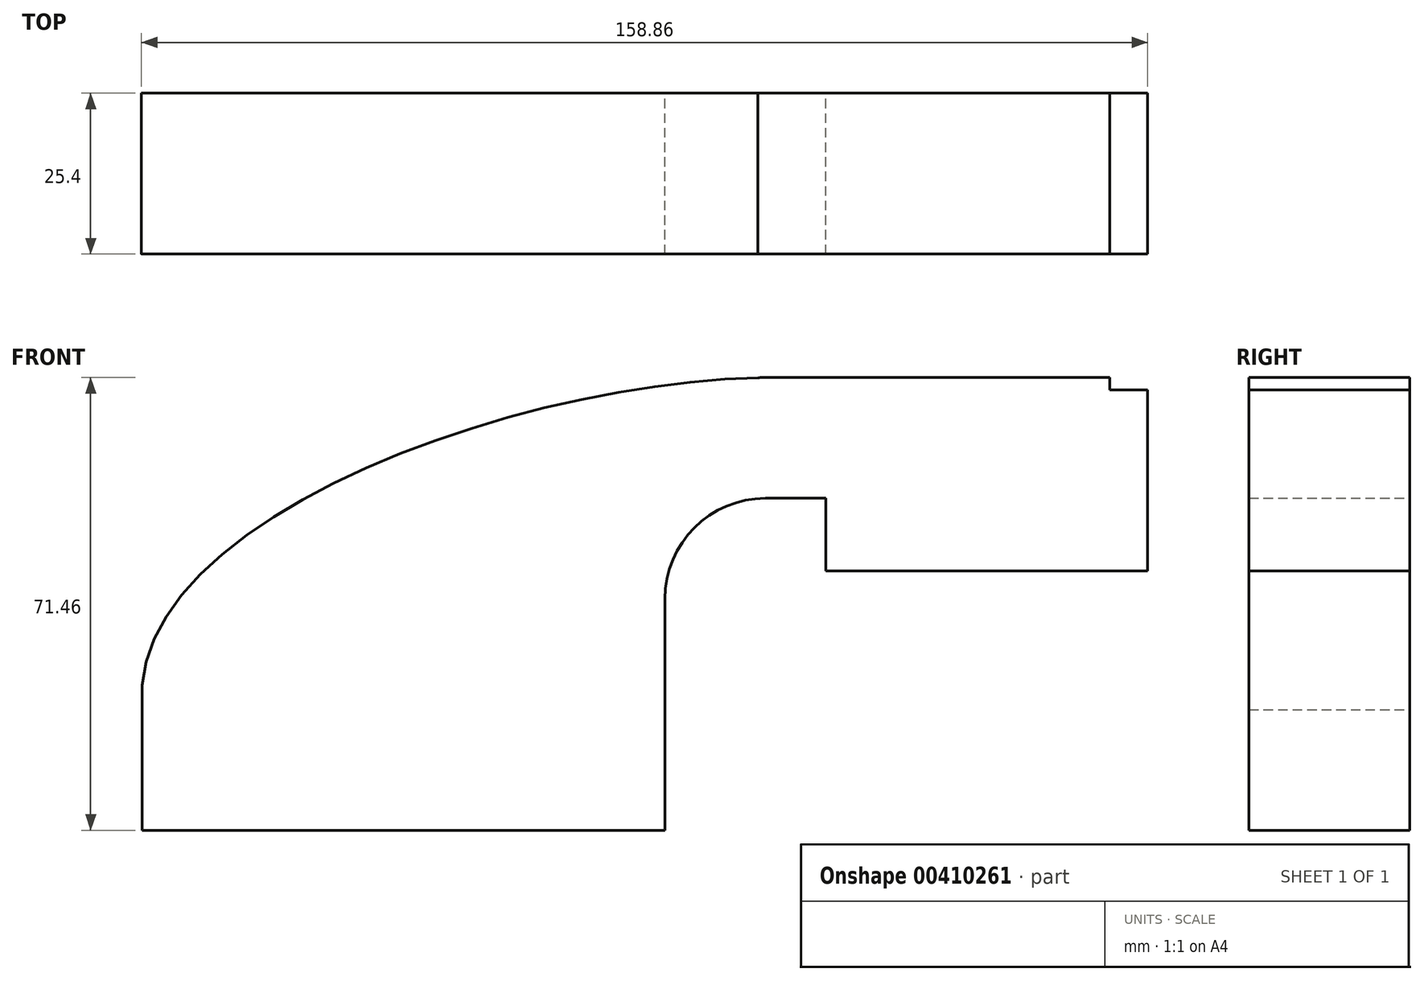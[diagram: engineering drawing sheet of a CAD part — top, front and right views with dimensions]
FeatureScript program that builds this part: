
annotation { "Feature Type Name" : "Feature", "Feature Type Description" : "" }
export const myFeature = defineFeature(function(context is Context, id is Id, definition is map)
    precondition{}
    {
        {
            var Q0;
            Q0=qCreatedBy(makeId("Front.planeOp"),FACE);
            var sketch = newSketch(context, id + "F0", { "sketchPlane" : qUnion([Q0])});
            skLineSegment(sketch, "E0.bottom", {"start": v(41.27, 9.53) * mm, "end": v(-41.28, 9.53) * mm});
            skLineSegment(sketch, "E0.top", {"start": v(41.28, -9.52) * mm, "end": v(-41.27, -9.52) * mm});
            skLineSegment(sketch, "E0.left", {"start": v(41.28, 9.53) * mm, "end": v(41.28, -9.52) * mm});
            skLineSegment(sketch, "E0.right", {"start": v(-41.28, 9.53) * mm, "end": v(-41.27, -9.52) * mm});
            skPoint(sketch, "E0.middle", {"position": v(0, 0) * mm});
            skLineSegment(sketch, "E1", {"start": v(41.27, 9.53) * mm, "end": v(41.27, 27) * mm});
            skLineSegment(sketch, "E2", {"start": v(57.15, 42.88) * mm, "end": v(111.51, 42.88) * mm});
            skArc(sketch, "E3", {"start": v(41.27, 27) * mm, "mid": v(45.92, 38.23) * mm, "end": v(57.15, 42.88) * mm});
            skLineSegment(sketch, "E4.bottom", {"start": v(117.47, 59.95) * mm, "end": v(66.67, 59.95) * mm});
            skLineSegment(sketch, "E4.top", {"start": v(117.47, 31.38) * mm, "end": v(66.67, 31.38) * mm});
            skLineSegment(sketch, "E4.left", {"start": v(117.47, 59.95) * mm, "end": v(117.47, 31.38) * mm});
            skLineSegment(sketch, "E4.right", {"start": v(66.67, 59.95) * mm, "end": v(66.67, 31.38) * mm});
            skLineSegment(sketch, "E5.0", {"start": v(57.15, 61.93) * mm, "end": v(111.51, 61.93) * mm});
            skArc(sketch, "E5.1", {"start": v(22.23, 27) * mm, "mid": v(32.45, 51.7) * mm, "end": v(57.15, 61.93) * mm});
            skLineSegment(sketch, "E5.2", {"start": v(22.22, 9.53) * mm, "end": v(22.22, 27) * mm});
            skLineSegment(sketch, "E6", {"start": v(22.22, 9.53) * mm, "end": v(41.27, 9.53) * mm});
            skLineSegment(sketch, "E7", {"start": v(111.51, 42.88) * mm, "end": v(111.51, 61.93) * mm});
            skFitSpline(sketch, "E8", {"points": [v(-41.28, 9.52) * mm, v(57.15, 61.93) * mm], "startDerivative": vector(-9, 89.63) * mm, "endDerivative": vector(117.72, 1.37) * mm});
            skSolve(sketch);
        }
        {
            var Q0;
            Q0 = qSketchRegion(id + "F0", true);
            extrude(context, id + "F1", {"entities" : qUnion([Q0]), "depth" : 25.4 * mm});
        }
    });
